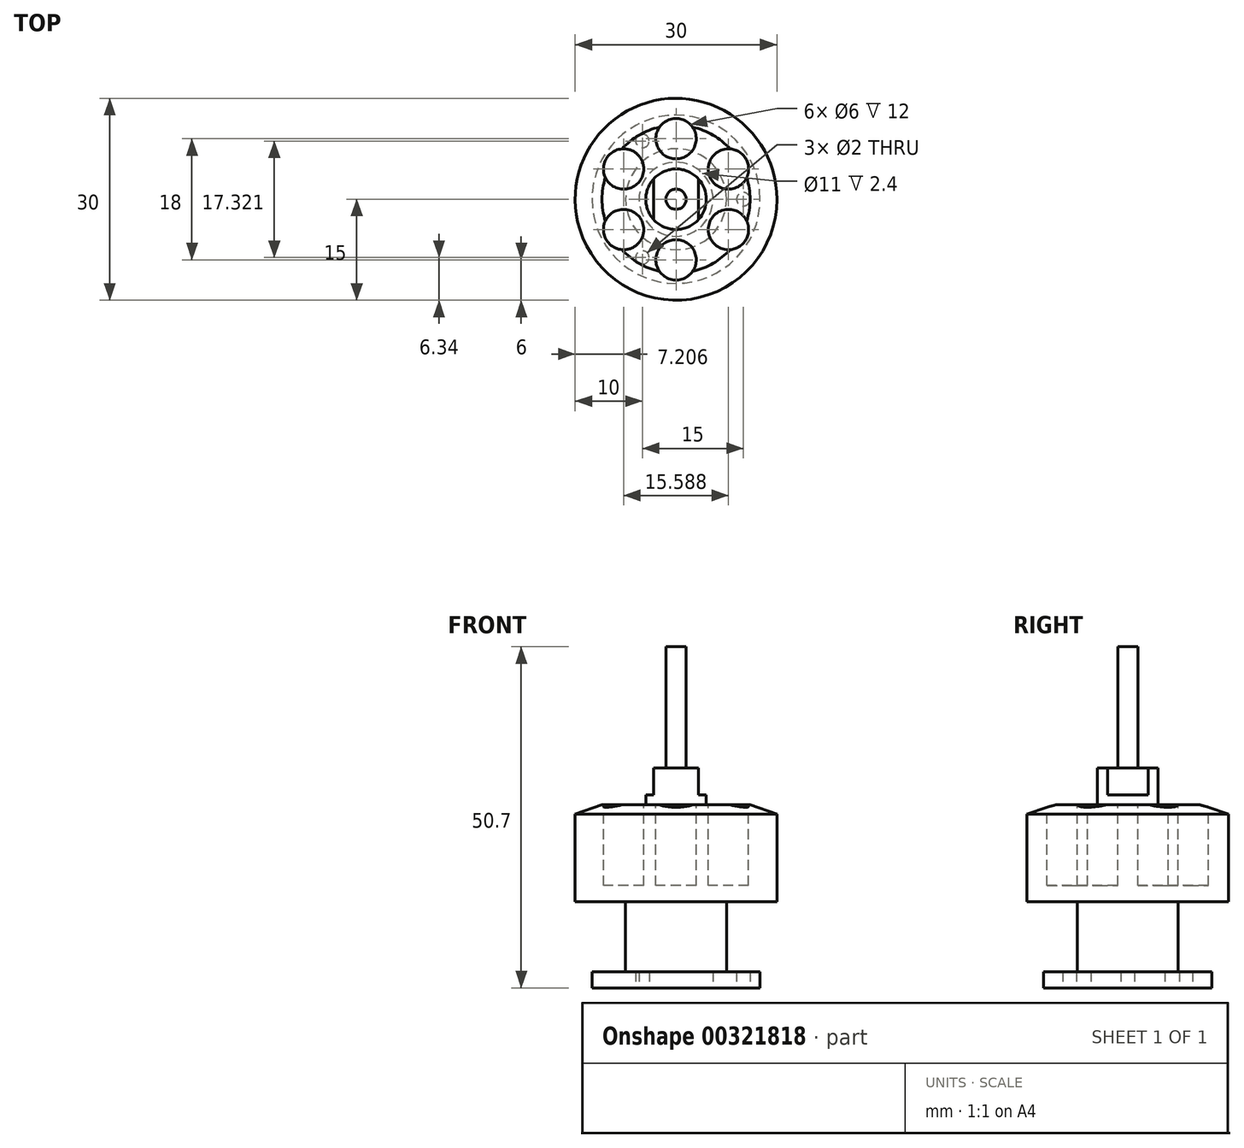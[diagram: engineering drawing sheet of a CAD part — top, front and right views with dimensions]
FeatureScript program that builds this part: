
annotation { "Feature Type Name" : "Feature", "Feature Type Description" : "" }
export const myFeature = defineFeature(function(context is Context, id is Id, definition is map)
    precondition{}
    {
        {
            var Q0;
            Q0=qCreatedBy(makeId("Top.planeOp"),FACE);
            var sketch = newSketch(context, id + "F0", { "sketchPlane" : qUnion([Q0])});
            skCircle(sketch, "E0", {"center": v(0, 0) * mm, "radius": 15 * mm});
            skSolve(sketch);
        }
        {
            var Q0;
            Q0 = qSketchRegion(id + "F0", true);
            extrude(context, id + "F1", {"entities" : qUnion([Q0]), "depth" : 12 * mm});
        }
        {
            var Q0;
            Q0=qCreatedBy(makeId("Front.planeOp"),FACE);
            var sketch = newSketch(context, id + "F2", { "sketchPlane" : qUnion([Q0])});
            skLineSegment(sketch, "E1", {"start": v(0, 14.4) * mm, "end": v(0, 12) * mm});
            skLineSegment(sketch, "E2", {"start": v(0, 12) * mm, "end": v(15, 12) * mm});
            skLineSegment(sketch, "E3", {"start": v(11, 14.4) * mm, "end": v(0, 14.4) * mm});
            skLineSegment(sketch, "E4", {"start": v(11, 14.4) * mm, "end": v(15, 13) * mm});
            skLineSegment(sketch, "E5", {"start": v(15, 13) * mm, "end": v(15, 12) * mm});
            skSolve(sketch);
        }
        {
            var Q0;
            Q0=makeQuery(id+"F2.imprint","IMPRINT",FACE,{"disambiguationData":[TD([[makeQuery(id+"F2.imprint","IMPRINT",EDGE,{"derivedFrom":sQuery(id+"F2.wireOp",EDGE,"E1")}),1.0]])]});
            var Q1;
            Q1=sQuery(id+"F2.wireOp",EDGE,"E1");
            revolve(context, id + "F3", {"operationType" : NewBodyOperationType.ADD, "entities" : qUnion([Q0]), "axis" : qUnion([Q1]), "revolveType" : RevolveType.FULL});
        }
        {
            var Q0;
            Q0=makeQuery(id+"F3.opRevolve","SWEPT_FACE",FACE,{"disambiguationData":[OSD([sQuery(id+"F2.wireOp",EDGE,"E3")])]});
            var sketch = newSketch(context, id + "F4", { "sketchPlane" : qUnion([Q0])});
            skCircle(sketch, "E6", {"center": v(0, 9) * mm, "radius": 3 * mm});
            skCircle(sketch, "E7.1.0", {"center": v(-7.8, 4.5) * mm, "radius": 3 * mm});
            skCircle(sketch, "E7.2.0", {"center": v(-7.8, -4.5) * mm, "radius": 3 * mm});
            skCircle(sketch, "E7.3.0", {"center": v(0, -9) * mm, "radius": 3 * mm});
            skCircle(sketch, "E7.4.0", {"center": v(7.8, -4.5) * mm, "radius": 3 * mm});
            skCircle(sketch, "E7.5.0", {"center": v(7.8, 4.5) * mm, "radius": 3 * mm});
            skPoint(sketch, "E7.center", {"position": v(0, 0) * mm});
            skSolve(sketch);
        }
        {
            var Q0;
            Q0 = qSketchRegion(id + "F4", true);
            extrude(context, id + "F5", {"entities" : qUnion([Q0]), "operationType" : NewBodyOperationType.REMOVE, "oppositeDirection" : true, "depth" : 12 * mm});
        }
        {
            var Q0;
            Q0=makeQuery(id+"F3.opRevolve","SWEPT_FACE",FACE,{"disambiguationData":[OSD([sQuery(id+"F2.wireOp",EDGE,"E3")])]});
            var sketch = newSketch(context, id + "F6", { "sketchPlane" : qUnion([Q0])});
            skCircle(sketch, "E8", {"center": v(0, 0) * mm, "radius": 4.5 * mm});
            skSolve(sketch);
        }
        {
            var Q0;
            Q0 = qSketchRegion(id + "F6", true);
            extrude(context, id + "F7", {"entities" : qUnion([Q0]), "operationType" : NewBodyOperationType.ADD, "depth" : 1.5 * mm});
        }
        {
            var Q0;
            Q0=makeQuery(id+"F7.opExtrude","CAP_FACE",FACE,{"disambiguationData":[OSD([sQuery(id+"F6.wireOp",EDGE,"E8")])],"isStart":false});
            var sketch = newSketch(context, id + "F8", { "sketchPlane" : qUnion([Q0])});
            skCircle(sketch, "E9", {"center": v(0, 0) * mm, "radius": 4.5 * mm});
            skLineSegment(sketch, "E10", {"start": v(3.35, 3) * mm, "end": v(3.35, -3) * mm});
            skLineSegment(sketch, "E11", {"start": v(-3.35, 3) * mm, "end": v(-3.35, -3) * mm});
            skSolve(sketch);
        }
        {
            var Q0;
            {var subQ0=sQuery(id+"F8.wireOp",EDGE,"E10");Q0=makeQuery(id+"F8.imprint","IMPRINT",FACE,{"disambiguationData":[TD([[makeQuery(id+"F8.imprint","IMPRINT",EDGE,{"derivedFrom":subQ0}),-1.0]])]});}
            extrude(context, id + "F9", {"entities" : qUnion([Q0]), "operationType" : NewBodyOperationType.ADD, "depth" : 4 * mm});
        }
        {
            var Q0;
            Q0=makeQuery(id+"F9.opExtrude","CAP_FACE",FACE,{"disambiguationData":[OSD([sQuery(id+"F8.wireOp",EDGE,"E9"),sQuery(id+"F8.wireOp",EDGE,"E10"),sQuery(id+"F8.wireOp",EDGE,"E11")])],"isStart":false});
            var sketch = newSketch(context, id + "F10", { "sketchPlane" : qUnion([Q0])});
            skCircle(sketch, "E12", {"center": v(0, 0) * mm, "radius": 1.5 * mm});
            skSolve(sketch);
        }
        {
            var Q0;
            Q0 = qSketchRegion(id + "F10", true);
            extrude(context, id + "F11", {"entities" : qUnion([Q0]), "operationType" : NewBodyOperationType.ADD, "depth" : 18 * mm});
        }
        {
            var Q0;
            Q0=makeQuery(id+"F1.opExtrude","CAP_FACE",FACE,{"disambiguationData":[OSD([sQuery(id+"F0.wireOp",EDGE,"E0")])],"isStart":true});
            var sketch = newSketch(context, id + "F12", { "sketchPlane" : qUnion([Q0])});
            skCircle(sketch, "E13", {"center": v(0, 0) * mm, "radius": 7.5 * mm});
            skSolve(sketch);
        }
        {
            var Q0;
            Q0 = qSketchRegion(id + "F12", true);
            extrude(context, id + "F13", {"entities" : qUnion([Q0]), "operationType" : NewBodyOperationType.ADD, "depth" : 10.4 * mm});
        }
        {
            var Q0;
            Q0=makeQuery(id+"F13.opExtrude","CAP_FACE",FACE,{"disambiguationData":[OSD([sQuery(id+"F12.wireOp",EDGE,"E13")])],"isStart":false});
            var sketch = newSketch(context, id + "F14", { "sketchPlane" : qUnion([Q0])});
            skCircle(sketch, "E14", {"center": v(0, 0) * mm, "radius": 12.5 * mm});
            skSolve(sketch);
        }
        {
            var Q0;
            Q0 = qSketchRegion(id + "F14", true);
            extrude(context, id + "F15", {"entities" : qUnion([Q0]), "operationType" : NewBodyOperationType.ADD, "depth" : 2.4 * mm});
        }
        {
            var Q0;
            Q0=makeQuery(id+"F15.opExtrude","CAP_FACE",FACE,{"disambiguationData":[OSD([sQuery(id+"F14.wireOp",EDGE,"E14")])],"isStart":false});
            var sketch = newSketch(context, id + "F16", { "sketchPlane" : qUnion([Q0])});
            skCircle(sketch, "E15", {"center": v(0, 0) * mm, "radius": 5.5 * mm});
            skCircle(sketch, "E16", {"center": v(0, 0) * mm, "radius": 10 * mm, "construction": true});
            skCircle(sketch, "E17", {"center": v(10, 0) * mm, "radius": 1 * mm});
            skCircle(sketch, "E18.1.0", {"center": v(-5, 8.66) * mm, "radius": 1 * mm});
            skCircle(sketch, "E18.2.0", {"center": v(-5, -8.66) * mm, "radius": 1 * mm});
            skSolve(sketch);
        }
        {
            var Q0;
            Q0 = qSketchRegion(id + "F16", true);
            extrude(context, id + "F17", {"entities" : qUnion([Q0]), "operationType" : NewBodyOperationType.REMOVE, "oppositeDirection" : true, "depth" : 2.4 * mm});
        }
    });
